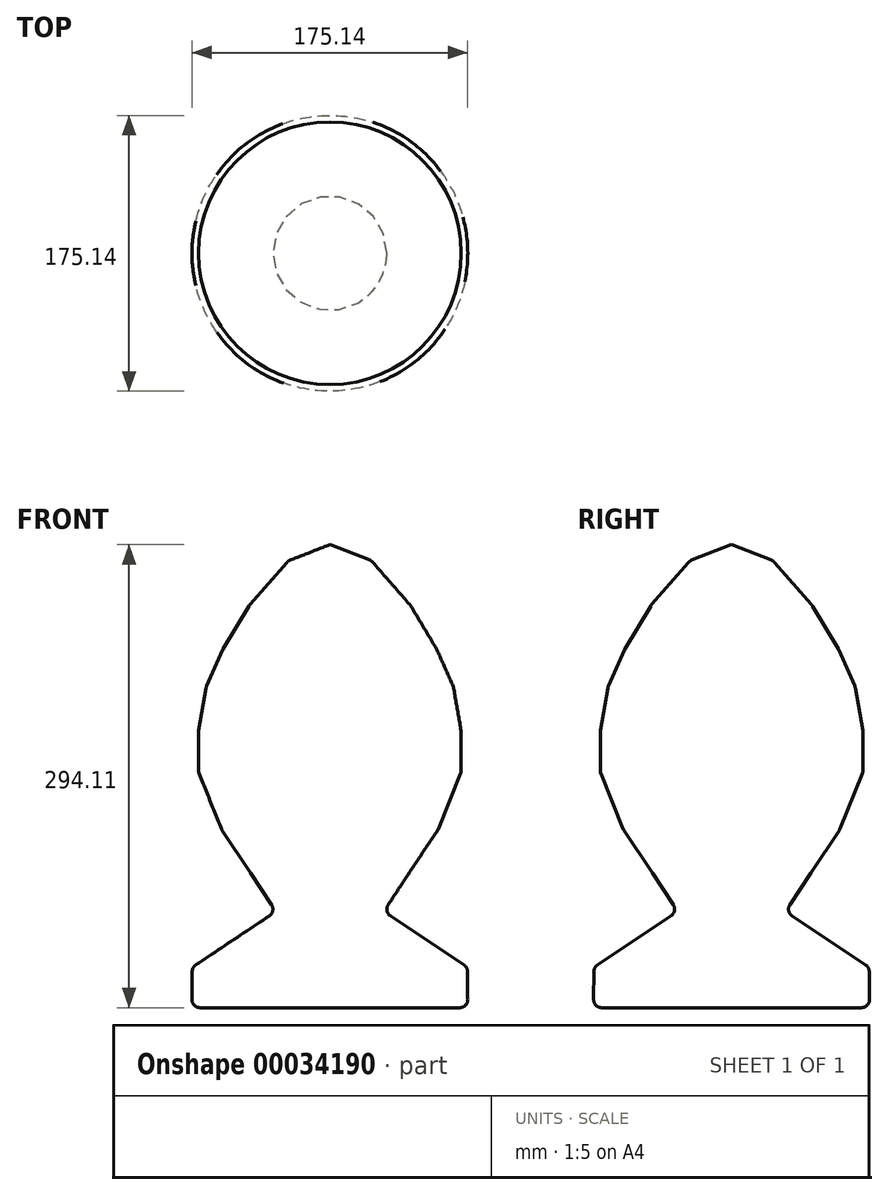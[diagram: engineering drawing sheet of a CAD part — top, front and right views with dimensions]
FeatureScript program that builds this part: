
annotation { "Feature Type Name" : "Feature", "Feature Type Description" : "" }
export const myFeature = defineFeature(function(context is Context, id is Id, definition is map)
    precondition{}
    {
        {
            var Q0;
            Q0=qCreatedBy(makeId("Front.planeOp"),FACE);
            var sketch = newSketch(context, id + "F0", { "sketchPlane" : qUnion([Q0])});
            skLineSegment(sketch, "E0", {"start": v(0, 294.11) * mm, "end": v(0, 0) * mm});
            skLineSegment(sketch, "E1", {"start": v(87.62, 0) * mm, "end": v(0, 0) * mm});
            skLineSegment(sketch, "E2", {"start": v(0, 294.11) * mm, "end": v(26.5, 283.76) * mm});
            skLineSegment(sketch, "E3", {"start": v(26.5, 283.76) * mm, "end": v(51.09, 255.66) * mm});
            skLineSegment(sketch, "E4", {"start": v(51.09, 255.66) * mm, "end": v(67.95, 227.56) * mm});
            skLineSegment(sketch, "E5", {"start": v(67.95, 227.56) * mm, "end": v(78.48, 203.68) * mm});
            skLineSegment(sketch, "E6", {"start": v(78.48, 203.68) * mm, "end": v(83.4, 175.58) * mm});
            skLineSegment(sketch, "E7", {"start": v(83.4, 175.58) * mm, "end": v(83.4, 149.6) * mm});
            skLineSegment(sketch, "E8", {"start": v(83.4, 149.6) * mm, "end": v(68.65, 113.07) * mm});
            skLineSegment(sketch, "E9", {"start": v(68.65, 113.07) * mm, "end": v(50.39, 85.67) * mm});
            skLineSegment(sketch, "E10", {"start": v(50.39, 85.67) * mm, "end": v(34.23, 61.08) * mm});
            skLineSegment(sketch, "E11", {"start": v(34.23, 61.08) * mm, "end": v(87.4, 25.64) * mm});
            skLineSegment(sketch, "E12", {"start": v(87.4, 25.64) * mm, "end": v(87.62, 0) * mm});
            skSolve(sketch);
        }
        {
            var Q0;
            Q0 = qSketchRegion(id + "F0", true);
            var Q1;
            Q1=sQuery(id+"F0.wireOp",EDGE,"E0");
            revolve(context, id + "F1", {"entities" : qUnion([Q0]), "axis" : qUnion([Q1]), "revolveType" : RevolveType.FULL});
        }
        {
            var Q0;
            Q0=makeQuery(id+"F1.opRevolve","SWEPT_EDGE",EDGE,{"disambiguationData":[OSD([sQuery(id+"F0.wireOp",EDGE,"E3"),sQuery(id+"F0.wireOp",EDGE,"E4")])]});
            var Q1;
            Q1=makeQuery(id+"F1.opRevolve","SWEPT_EDGE",EDGE,{"disambiguationData":[OSD([sQuery(id+"F0.wireOp",EDGE,"E4"),sQuery(id+"F0.wireOp",EDGE,"E5")])]});
            var Q2;
            Q2=makeQuery(id+"F1.opRevolve","SWEPT_EDGE",EDGE,{"disambiguationData":[OSD([sQuery(id+"F0.wireOp",EDGE,"E6"),sQuery(id+"F0.wireOp",EDGE,"E7")])]});
            var Q3;
            Q3=makeQuery(id+"F1.opRevolve","SWEPT_EDGE",EDGE,{"disambiguationData":[OSD([sQuery(id+"F0.wireOp",EDGE,"E5"),sQuery(id+"F0.wireOp",EDGE,"E6")])]});
            var Q4;
            Q4=makeQuery(id+"F1.opRevolve","SWEPT_EDGE",EDGE,{"disambiguationData":[OSD([sQuery(id+"F0.wireOp",EDGE,"E7"),sQuery(id+"F0.wireOp",EDGE,"E8")])]});
            var Q5;
            Q5=makeQuery(id+"F1.opRevolve","SWEPT_EDGE",EDGE,{"disambiguationData":[OSD([sQuery(id+"F0.wireOp",EDGE,"E2"),sQuery(id+"F0.wireOp",EDGE,"E3")])]});
            var Q6;
            Q6=makeQuery(id+"F1.opRevolve","SWEPT_EDGE",EDGE,{"disambiguationData":[OSD([sQuery(id+"F0.wireOp",EDGE,"E8"),sQuery(id+"F0.wireOp",EDGE,"E9")])]});
            var Q7;
            Q7=makeQuery(id+"F1.opRevolve","SWEPT_EDGE",EDGE,{"disambiguationData":[OSD([sQuery(id+"F0.wireOp",EDGE,"E9"),sQuery(id+"F0.wireOp",EDGE,"E10")])]});
            var Q8;
            Q8=makeQuery(id+"F1.opRevolve","SWEPT_EDGE",EDGE,{"disambiguationData":[OSD([sQuery(id+"F0.wireOp",EDGE,"E10"),sQuery(id+"F0.wireOp",EDGE,"E11")])]});
            var Q9;
            Q9=makeQuery(id+"F1.opRevolve","SWEPT_EDGE",EDGE,{"disambiguationData":[OSD([sQuery(id+"F0.wireOp",EDGE,"E11"),sQuery(id+"F0.wireOp",EDGE,"E12")])]});
            var Q10;
            Q10=makeQuery(id+"F1.opRevolve","SWEPT_EDGE",EDGE,{"disambiguationData":[OSD([sQuery(id+"F0.wireOp",EDGE,"E1"),sQuery(id+"F0.wireOp",EDGE,"E12")])]});
            fillet(context, id + "F2", {"entities" : qUnion([Q0, Q1, Q2, Q3, Q4, Q5, Q6, Q7, Q8, Q9, Q10]), "radius" : 5.08 * mm, "tangentPropagation" : true, "allowEdgeOverflow" : false});
        }
    });
